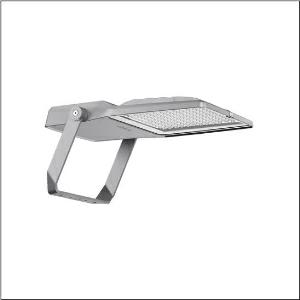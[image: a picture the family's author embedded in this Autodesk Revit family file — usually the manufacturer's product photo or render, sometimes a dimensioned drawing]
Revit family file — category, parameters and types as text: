
# Revit family: floodlight_fl_21_midi___pl43_5xa7786e4a1a_b497
name_source: partatom
category: Lighting Fixtures
units: mm (PartAtom-declared; Revit-internal decimal feet)

## family parameters
Cut with Voids When Loaded = No
Host = Face
Light Source = No
Part Type = Normal
Room Calculation Point = No
Round Connector Dimension = Use Diameter
Shared = No

## types (1)
- --- (1 x LED, 28830 lm, 212.4 W, 4000K)
    Apparent Load = 212 VA
    CIE Flux Codes = 27 78 99 100 100
    Color Rendering = 70
    Color Temperature = 4000K
    Default Elevation = 1800 mm
    Description = Floodlight FL 21 midi, floodlight, primary light control with lens, of PMMA, primary optical cover: protective disc, of toughened safety glass, transparent, light distribution: PL43, light emission: direct distribution, installation type: surface-mounted, LED, High Power LED, rated luminous flux: 28.830lm, luminous efficacy: 136lm/W, light colour: 740, colour temperature: 4000K, control gear: Smart Interface (Zhaga)D4i, control: overheat protection, constant luminous flux control, time-dependent luminous flux control, flexible luminous flux parameterisation, pre-setting: logarithmic dimming characteristic, with terminal, 6-pole, mains connection: 220..240V, AC, 50/60Hz, start of lifetime: 212W, end of service life: 231W, reduction: 95W, mounting bracket, of diecast aluminium, powder-coated, SITECO metallic grey (DB 702S), corrosivity category C5 mid according to DIN EN ISO 12944, suitable for swimming pools, chlorine-resistant, sealing non-destructively replaceable, mounting bracket, of steel, galvanised, powder-coated, SITECO metallic grey (DB 702S), Smart Interface below and above, protection rating (complete): IP66, insulation class (complete): insulation class II (safety insulation), certification: CE, ENEC, VDE, protection symbol: D, impact resistance: IK08, permissible operating ambient temperature: -40..+40°C, permissible operating ambient temperature for outdoor applications: -40..+50°C, standard: DIN EN 12944, LABS conformity tested according to VDMA 24364:2018-05, packaging unit: 1 piece

Light Distribution: PL43
    Height = 76 mm
    Lamp = 1 x LED
    Lamp Light Flux = 28830 lm
    Lamp Power = 212.4 W
    Lamp count = 1
    Length = 657 mm
    Luminous efficacy = 136 lm/W
    Manufacturer = Siteco
    ModVariant = No
    Model = 5XA7786E4A1A
    Mounting Place = Pole
    Mounting Type = Pole annexe
    Number of Poles = 1
    OnlyDefault = Yes
    Power Factor = 1
    Product Name = Floodlight FL 21 midi | PL43
    Product group = floodlight | pylon annexe
    ProductGroupID = 6201
    Protection Class = Protection class II
    Protection Degree = IP 66
    RLX_Detail_Level = 1
    RLX_Emergency_Light_Flux = 0 lm
    RLX_Emergency_Type = 0
    RLX_Emergency_Type_DB = No
    RlxData = <blob elided: 101569 chars, md5=1bfd62cc>
    Socket = socket
    Standby Power = 0 W
    System Light Flux = 28830 lm
    System Power = 212 W
    Type Comments = factory setting: luminous flux: 100 % | dim-lin: 254 | 710 mA
    Type Image = l_1006876.jpg
    URL = http://relux.com
    VarID = @adj_094625
    Voltage = 0 V
    Weight = 0.00 kg
    Width = 442 mm

## geometry (parser evidence)
native form markers: Blend x4, Sweep x11
no freeform markers — native parametric forms only
